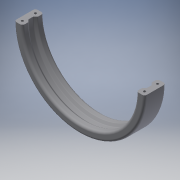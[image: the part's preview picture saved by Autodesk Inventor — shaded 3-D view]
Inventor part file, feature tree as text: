
AUTODESK INVENTOR PART (.ipt)
format: ipt  version: 2016 (Build 200138000, 138)  size: 251,392 bytes
history: native  units: mm
features: fillet x5, sketch x4, extrude x3, revolve x1, plane x1
ambient origin geometry x8: Origin, YZ Plane, XZ Plane, XY Plane, X Axis, Y Axis, Z Axis, Center Point
bodies: Solid1 (feature_tree)
feature tree (14):
  revolve  "Revolution1"  [1 undecoded]
  plane  "Work Plane1"
  extrude  "Extrusion1"  Depth=7.0mm
  fillet  "Fillet1"  Radius=5.0mm
  fillet  "Fillet2"  [1 undecoded]
  fillet  "Fillet3"  Radius=50.0mm
  fillet  "Fillet4"  Radius=18.0mm
  fillet  "Fillet5"  Radius=100.0mm
  extrude  "Extrusion2"  Depth=2.0mm
  extrude  "Extrusion3"  Depth=2.0mm
  sketch  "Sketch1"  dims[d0=50.0mm d1=9.0mm]
  sketch  "Sketch2"  dims[d2=5.0mm d3=7.0mm d4=5.0mm d5=90.0deg d6=50.0mm d7=18.0mm d8=100.0mm d9=0.0mm]
  sketch  "Sketch3"  dims[d10=4.0mm d11=2.0mm]
  sketch  "Sketch4"  dims[d12=2.0mm d13=2.0mm d14=1.0mm d15=20.0mm d16=0.0mm d17=3.5mm d18=1.984375mm d19=1.984375mm d20=3.5mm d21=3.5mm d22=6.985mm d23=0.0mm]
note: 2 required parameter values undecoded (feature->parameter linkage not recoverable at this tier; creation-order binding heuristic only, values carry confidence <= 0.55)